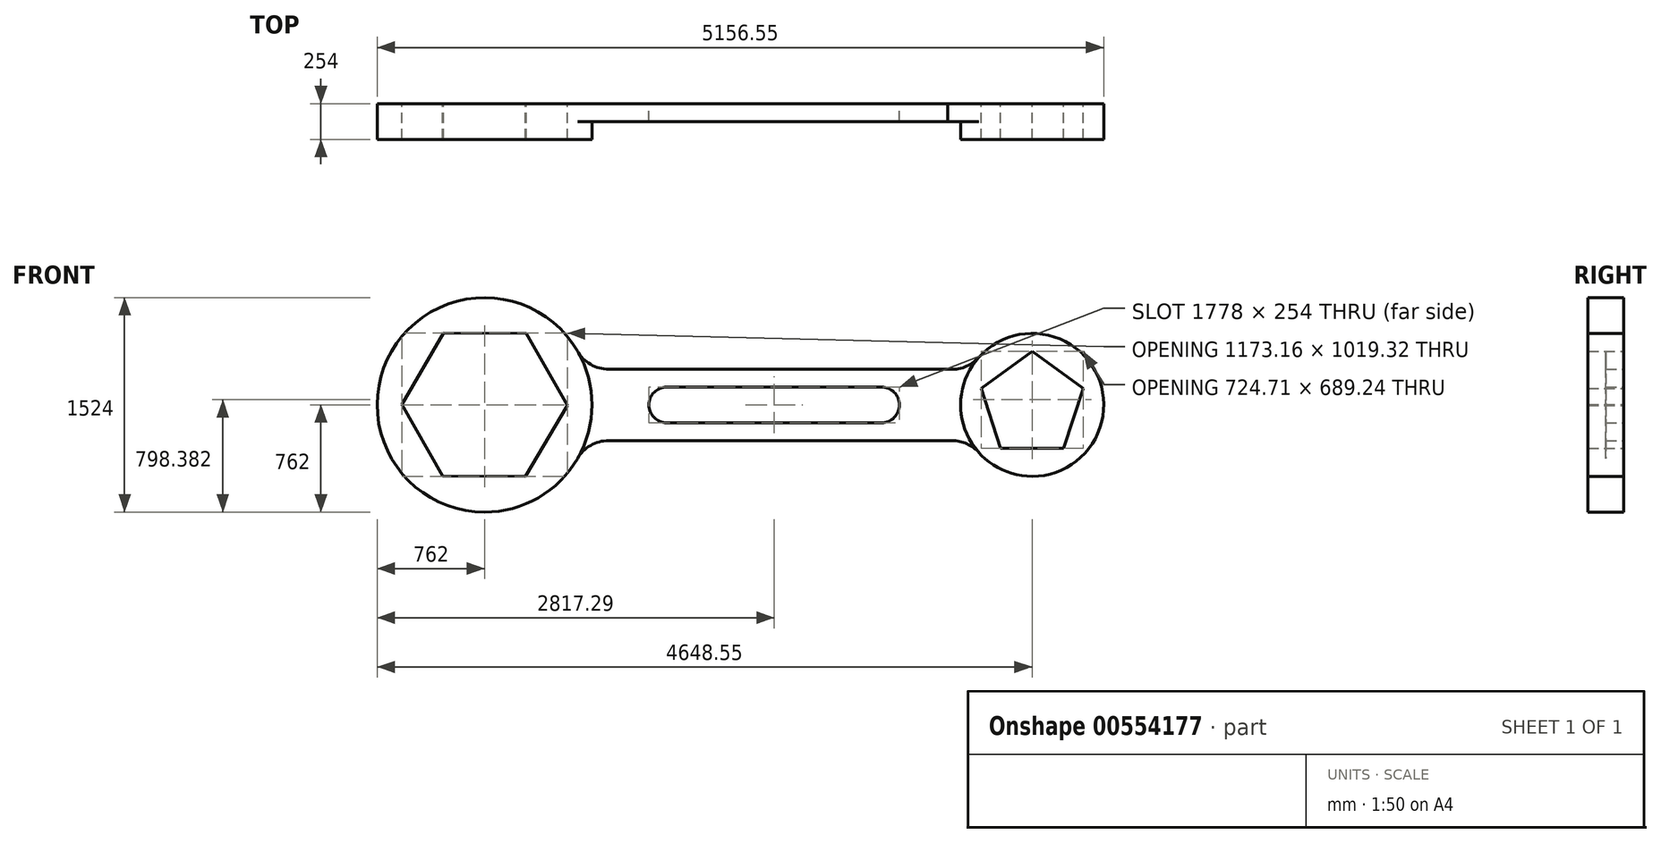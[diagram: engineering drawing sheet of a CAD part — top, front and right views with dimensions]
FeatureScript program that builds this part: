
annotation { "Feature Type Name" : "Feature", "Feature Type Description" : "" }
export const myFeature = defineFeature(function(context is Context, id is Id, definition is map)
    precondition{}
    {
        {
            var Q0;
            Q0=qCreatedBy(makeId("Front.planeOp"),FACE);
            var sketch = newSketch(context, id + "F0", { "sketchPlane" : qUnion([Q0])});
            skCircle(sketch, "E0", {"center": v(0, 0) * mm, "radius": 762 * mm});
            skLineSegment(sketch, "E1", {"start": v(1166.3, 0) * mm, "end": v(2944.3, 0) * mm});
            skCircle(sketch, "E2", {"center": v(3886.55, 0) * mm, "radius": 508 * mm});
            skLineSegment(sketch, "E3", {"start": v(2070.27, 0) * mm, "end": v(2070.27, 127) * mm});
            skLineSegment(sketch, "E4", {"start": v(2070.27, 127) * mm, "end": v(1293.3, 127) * mm});
            skLineSegment(sketch, "E5", {"start": v(1293.3, -127) * mm, "end": v(2817.3, -127) * mm});
            skLineSegment(sketch, "E6", {"start": v(2817.3, 127) * mm, "end": v(2070.27, 127) * mm});
            skLineSegment(sketch, "E7", {"start": v(1166.3, 0) * mm, "end": v(1293.3, 0) * mm});
            skArc(sketch, "E8", {"start": v(1293.3, 127) * mm, "mid": v(1166.3, 0) * mm, "end": v(1293.3, -127) * mm});
            skLineSegment(sketch, "E9", {"start": v(2944.3, 0) * mm, "end": v(2817.3, 0) * mm});
            skArc(sketch, "E10", {"start": v(2817.3, -127) * mm, "mid": v(2944.3, 0) * mm, "end": v(2817.3, 127) * mm});
            skPoint(sketch, "E11.orphan", {"position": v(1166.3, -127) * mm});
            skPoint(sketch, "E12.orphan", {"position": v(1166.3, 127) * mm});
            skPoint(sketch, "E13.orphan", {"position": v(2944.3, 127) * mm});
            skPoint(sketch, "E14.orphan", {"position": v(2944.3, -127) * mm});
            skLineSegment(sketch, "E15", {"start": v(2070.27, 0) * mm, "end": v(2070.27, -254) * mm});
            skLineSegment(sketch, "E16", {"start": v(2070.27, -254) * mm, "end": v(879.88, -254) * mm});
            skLineSegment(sketch, "E17", {"start": v(2070.27, -254) * mm, "end": v(3318.59, -254) * mm});
            skLineSegment(sketch, "E18", {"start": v(2070.27, 0) * mm, "end": v(2070.27, 254) * mm});
            skPoint(sketch, "E18.endSnap0", {"position": v(2070.27, 63.5) * mm});
            skLineSegment(sketch, "E19", {"start": v(2070.27, 254) * mm, "end": v(879.88, 254) * mm});
            skLineSegment(sketch, "E20", {"start": v(2070.27, 254) * mm, "end": v(3346.2, 254) * mm});
            skArc(sketch, "E21", {"start": v(659.91, 381) * mm, "mid": v(752.88, 288.03) * mm, "end": v(879.88, 254) * mm});
            skArc(sketch, "E22", {"start": v(879.88, -254) * mm, "mid": v(752.88, -288.03) * mm, "end": v(659.91, -381) * mm});
            skArc(sketch, "E23", {"start": v(3287.98, 254) * mm, "mid": v(3407.66, 269.02) * mm, "end": v(3506.91, 337.55) * mm});
            skArc(sketch, "E24", {"start": v(3507.9, -338.67) * mm, "mid": v(3422.28, -276.13) * mm, "end": v(3318.59, -254) * mm});
            skCircle(sketch, "E25.cCircle", {"center": v(0, 0) * mm, "radius": 508 * mm, "construction": true});
            skLineSegment(sketch, "E25.0", {"start": v(-586.58, 3.33) * mm, "end": v(-290.4, 509.66) * mm});
            skLineSegment(sketch, "E25.1", {"start": v(-290.4, 509.66) * mm, "end": v(296.17, 506.33) * mm});
            skLineSegment(sketch, "E25.2", {"start": v(296.17, 506.33) * mm, "end": v(586.58, -3.33) * mm});
            skLineSegment(sketch, "E25.3", {"start": v(586.58, -3.33) * mm, "end": v(290.4, -509.66) * mm});
            skLineSegment(sketch, "E25.4", {"start": v(290.4, -509.66) * mm, "end": v(-296.17, -506.33) * mm});
            skLineSegment(sketch, "E25.5", {"start": v(-296.17, -506.33) * mm, "end": v(-586.58, 3.33) * mm});
            skPoint(sketch, "E25.0.midPoint", {"position": v(-438.5, 256.5) * mm});
            skCircle(sketch, "E26.cCircle", {"center": v(3886.55, 0) * mm, "radius": 308.24 * mm, "construction": true});
            skLineSegment(sketch, "E26.0", {"start": v(4110.5, -308.24) * mm, "end": v(3662.6, -308.24) * mm});
            skLineSegment(sketch, "E26.1", {"start": v(3662.6, -308.24) * mm, "end": v(3524.2, 117.74) * mm});
            skLineSegment(sketch, "E26.2", {"start": v(3524.2, 117.74) * mm, "end": v(3886.55, 381) * mm});
            skLineSegment(sketch, "E26.3", {"start": v(3886.55, 381) * mm, "end": v(4248.9, 117.74) * mm});
            skLineSegment(sketch, "E26.4", {"start": v(4248.9, 117.74) * mm, "end": v(4110.5, -308.24) * mm});
            skPoint(sketch, "E26.0.midPoint", {"position": v(3886.55, -308.24) * mm});
            skPoint(sketch, "E27.orphan", {"position": v(762, 0) * mm});
            skPoint(sketch, "E28.orphan", {"position": v(3378.55, 0) * mm});
            skSolve(sketch);
        }
        {
            var Q0;
            {var subQ2=sQuery(id+"F0.wireOp",EDGE,"E4");Q0=makeQuery(id+"F0.imprint","IMPRINT",FACE,{"disambiguationData":[TD([[makeQuery(id+"F0.imprint","IMPRINT",EDGE,{"derivedFrom":subQ2}),-1.0]])]});}
            var Q1;
            {var subQ9=sQuery(id+"F0.wireOp",EDGE,"E6");Q1=makeQuery(id+"F0.imprint","IMPRINT",FACE,{"disambiguationData":[TD([[makeQuery(id+"F0.imprint","IMPRINT",EDGE,{"derivedFrom":subQ9}),-1.0]])]});}
            extrude(context, id + "F1", {"entities" : qUnion([Q0, Q1]), "depth" : 127 * mm, "offsetDistance" : 25.4 * mm});
        }
        {
            var Q0;
            Q0=makeQuery(id+"F0.imprint","IMPRINT",FACE,{"disambiguationData":[TD([[makeQuery(id+"F0.imprint","IMPRINT",EDGE,{"derivedFrom":sQuery(id+"F0.wireOp",EDGE,"E25.0")}),1.0]])]});
            var Q1;
            Q1=makeQuery(id+"F0.imprint","IMPRINT",FACE,{"disambiguationData":[TD([[makeQuery(id+"F0.imprint","IMPRINT",EDGE,{"derivedFrom":sQuery(id+"F0.wireOp",EDGE,"E26.0")}),1.0]])]});
            extrude(context, id + "F2", {"entities" : qUnion([Q0, Q1]), "operationType" : NewBodyOperationType.ADD, "depth" : 254 * mm, "offsetDistance" : 25.4 * mm});
        }
    });
